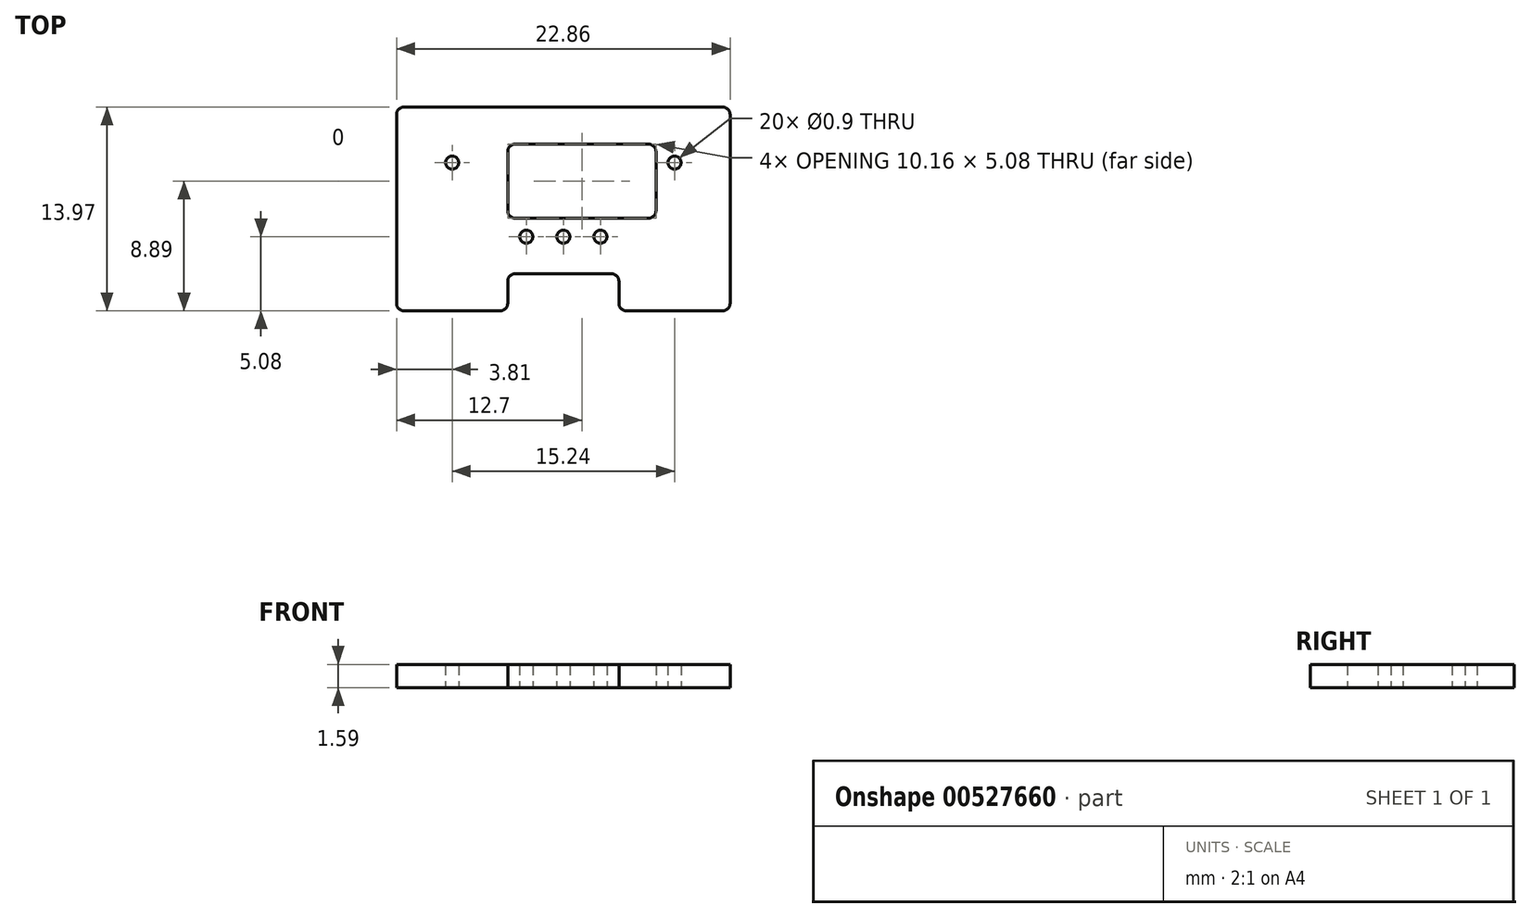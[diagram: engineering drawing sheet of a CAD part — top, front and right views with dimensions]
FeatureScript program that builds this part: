
annotation { "Feature Type Name" : "Feature", "Feature Type Description" : "" }
export const myFeature = defineFeature(function(context is Context, id is Id, definition is map)
    precondition{}
    {
        {
            var Q0;
            Q0=qCreatedBy(makeId("Top.planeOp"),FACE);
            var sketch = newSketch(context, id + "F0", { "sketchPlane" : qUnion([Q0])});
            skPoint(sketch, "E0", {"position": v(0, 0) * mm});
            skPoint(sketch, "E1.0.1.0", {"position": v(0, 2.54) * mm});
            skPoint(sketch, "E1.0.2.0", {"position": v(0, 5.08) * mm});
            skPoint(sketch, "E1.0.3.0", {"position": v(0, 7.62) * mm});
            skPoint(sketch, "E1.0.4.0", {"position": v(0, 10.16) * mm});
            skPoint(sketch, "E1.0.5.0", {"position": v(0, 12.7) * mm});
            skPoint(sketch, "E1.1.0.0", {"position": v(2.54, 0) * mm});
            skPoint(sketch, "E1.1.1.0", {"position": v(2.54, 2.54) * mm});
            skPoint(sketch, "E1.1.2.0", {"position": v(2.54, 5.08) * mm});
            skPoint(sketch, "E1.1.3.0", {"position": v(2.54, 7.62) * mm});
            skPoint(sketch, "E1.1.4.0", {"position": v(2.54, 10.16) * mm});
            skPoint(sketch, "E1.1.5.0", {"position": v(2.54, 12.7) * mm});
            skPoint(sketch, "E1.2.0.0", {"position": v(5.08, 0) * mm});
            skPoint(sketch, "E1.2.1.0", {"position": v(5.08, 2.54) * mm});
            skPoint(sketch, "E1.2.2.0", {"position": v(5.08, 5.08) * mm});
            skPoint(sketch, "E1.2.3.0", {"position": v(5.08, 7.62) * mm});
            skPoint(sketch, "E1.2.4.0", {"position": v(5.08, 10.16) * mm});
            skPoint(sketch, "E1.2.5.0", {"position": v(5.08, 12.7) * mm});
            skPoint(sketch, "E1.3.0.0", {"position": v(7.62, 0) * mm});
            skPoint(sketch, "E1.3.1.0", {"position": v(7.62, 2.54) * mm});
            skPoint(sketch, "E1.3.2.0", {"position": v(7.62, 5.08) * mm});
            skPoint(sketch, "E1.3.3.0", {"position": v(7.62, 7.62) * mm});
            skPoint(sketch, "E1.3.4.0", {"position": v(7.62, 10.16) * mm});
            skPoint(sketch, "E1.3.5.0", {"position": v(7.62, 12.7) * mm});
            skPoint(sketch, "E1.4.0.0", {"position": v(10.16, 0) * mm});
            skPoint(sketch, "E1.4.1.0", {"position": v(10.16, 2.54) * mm});
            skPoint(sketch, "E1.4.2.0", {"position": v(10.16, 5.08) * mm});
            skPoint(sketch, "E1.4.3.0", {"position": v(10.16, 7.62) * mm});
            skPoint(sketch, "E1.4.4.0", {"position": v(10.16, 10.16) * mm});
            skPoint(sketch, "E1.4.5.0", {"position": v(10.16, 12.7) * mm});
            skPoint(sketch, "E1.5.0.0", {"position": v(12.7, 0) * mm});
            skPoint(sketch, "E1.5.1.0", {"position": v(12.7, 2.54) * mm});
            skPoint(sketch, "E1.5.2.0", {"position": v(12.7, 5.08) * mm});
            skPoint(sketch, "E1.5.3.0", {"position": v(12.7, 7.62) * mm});
            skPoint(sketch, "E1.5.4.0", {"position": v(12.7, 10.16) * mm});
            skPoint(sketch, "E1.5.5.0", {"position": v(12.7, 12.7) * mm});
            skPoint(sketch, "E1.6.0.0", {"position": v(15.24, 0) * mm});
            skPoint(sketch, "E1.6.1.0", {"position": v(15.24, 2.54) * mm});
            skPoint(sketch, "E1.6.2.0", {"position": v(15.24, 5.08) * mm});
            skPoint(sketch, "E1.6.3.0", {"position": v(15.24, 7.62) * mm});
            skPoint(sketch, "E1.6.4.0", {"position": v(15.24, 10.16) * mm});
            skPoint(sketch, "E1.6.5.0", {"position": v(15.24, 12.7) * mm});
            skPoint(sketch, "E1.7.0.0", {"position": v(17.78, 0) * mm});
            skPoint(sketch, "E1.7.1.0", {"position": v(17.78, 2.54) * mm});
            skPoint(sketch, "E1.7.2.0", {"position": v(17.78, 5.08) * mm});
            skPoint(sketch, "E1.7.3.0", {"position": v(17.78, 7.62) * mm});
            skPoint(sketch, "E1.7.4.0", {"position": v(17.78, 10.16) * mm});
            skPoint(sketch, "E1.7.5.0", {"position": v(17.78, 12.7) * mm});
            skPoint(sketch, "E1.8.0.0", {"position": v(20.32, 0) * mm});
            skPoint(sketch, "E1.8.1.0", {"position": v(20.32, 2.54) * mm});
            skPoint(sketch, "E1.8.2.0", {"position": v(20.32, 5.08) * mm});
            skPoint(sketch, "E1.8.3.0", {"position": v(20.32, 7.62) * mm});
            skPoint(sketch, "E1.8.4.0", {"position": v(20.32, 10.16) * mm});
            skPoint(sketch, "E1.8.5.0", {"position": v(20.32, 12.7) * mm});
            skLineSegment(sketch, "E1.direction1", {"start": v(0, 0) * mm, "end": v(2.54, 0) * mm, "construction": true});
            skLineSegment(sketch, "E1.direction2", {"start": v(0, 0) * mm, "end": v(0, 2.54) * mm, "construction": true});
            skLineSegment(sketch, "E2.bottom", {"start": v(8.9, 6.35) * mm, "end": v(19.05, 6.35) * mm});
            skLineSegment(sketch, "E2.top", {"start": v(8.9, 11.43) * mm, "end": v(19.05, 11.43) * mm});
            skLineSegment(sketch, "E2.left", {"start": v(8.9, 6.35) * mm, "end": v(8.9, 11.43) * mm});
            skLineSegment(sketch, "E2.right", {"start": v(19.05, 6.35) * mm, "end": v(19.05, 11.43) * mm});
            skPoint(sketch, "E3", {"position": v(19.05, 5.08) * mm});
            skPoint(sketch, "E4", {"position": v(12.7, 6.35) * mm});
            skPoint(sketch, "E5", {"position": v(8.9, 5.08) * mm});
            skPoint(sketch, "E6", {"position": v(12.7, 11.43) * mm});
            skPoint(sketch, "E7.0.0.6", {"position": v(0, 15.24) * mm});
            skPoint(sketch, "E7.0.1.6", {"position": v(2.54, 15.24) * mm});
            skPoint(sketch, "E7.0.2.6", {"position": v(5.08, 15.24) * mm});
            skPoint(sketch, "E7.0.3.6", {"position": v(7.62, 15.24) * mm});
            skPoint(sketch, "E7.0.4.6", {"position": v(10.16, 15.24) * mm});
            skPoint(sketch, "E7.0.5.6", {"position": v(12.7, 15.24) * mm});
            skPoint(sketch, "E7.0.6.6", {"position": v(15.24, 15.24) * mm});
            skPoint(sketch, "E7.0.7.6", {"position": v(17.78, 15.24) * mm});
            skPoint(sketch, "E7.0.8.6", {"position": v(20.32, 15.24) * mm});
            skPoint(sketch, "E8.0.9.0", {"position": v(22.86, 0) * mm});
            skPoint(sketch, "E8.0.9.1", {"position": v(22.86, 2.54) * mm});
            skPoint(sketch, "E8.0.9.2", {"position": v(22.86, 5.08) * mm});
            skPoint(sketch, "E8.0.9.3", {"position": v(22.86, 7.62) * mm});
            skPoint(sketch, "E8.0.9.4", {"position": v(22.86, 10.16) * mm});
            skPoint(sketch, "E8.0.9.5", {"position": v(22.86, 12.7) * mm});
            skPoint(sketch, "E8.0.9.6", {"position": v(22.86, 15.24) * mm});
            skPoint(sketch, "E8.0.10.0", {"position": v(25.4, 0) * mm});
            skPoint(sketch, "E8.0.10.1", {"position": v(25.4, 2.54) * mm});
            skPoint(sketch, "E8.0.10.2", {"position": v(25.4, 5.08) * mm});
            skPoint(sketch, "E8.0.10.3", {"position": v(25.4, 7.62) * mm});
            skPoint(sketch, "E8.0.10.4", {"position": v(25.4, 10.16) * mm});
            skPoint(sketch, "E8.0.10.5", {"position": v(25.4, 12.7) * mm});
            skPoint(sketch, "E8.0.10.6", {"position": v(25.4, 15.24) * mm});
            skCircle(sketch, "E9", {"center": v(12.7, 5.08) * mm, "radius": 0.45 * mm});
            skCircle(sketch, "E10", {"center": v(10.16, 5.08) * mm, "radius": 0.45 * mm});
            skCircle(sketch, "E11", {"center": v(15.24, 5.08) * mm, "radius": 0.45 * mm});
            skCircle(sketch, "E12", {"center": v(20.32, 10.16) * mm, "radius": 0.45 * mm});
            skCircle(sketch, "E13", {"center": v(5.08, 10.16) * mm, "radius": 0.45 * mm});
            skLineSegment(sketch, "E14", {"start": v(10.16, 5.08) * mm, "end": v(7.62, 5.08) * mm, "construction": true});
            skLineSegment(sketch, "E15", {"start": v(20.32, 5.08) * mm, "end": v(17.78, 5.08) * mm, "construction": true});
            skLineSegment(sketch, "E16", {"start": v(12.7, 7.62) * mm, "end": v(12.7, 5.08) * mm, "construction": true});
            skLineSegment(sketch, "E17", {"start": v(12.7, 12.7) * mm, "end": v(12.7, 10.16) * mm, "construction": true});
            skLineSegment(sketch, "E18", {"start": v(25.4, 5.08) * mm, "end": v(22.86, 5.08) * mm, "construction": true});
            skLineSegment(sketch, "E19", {"start": v(2.54, 5.08) * mm, "end": v(0, 5.08) * mm, "construction": true});
            skLineSegment(sketch, "E20", {"start": v(12.7, 15.24) * mm, "end": v(12.7, 12.7) * mm, "construction": true});
            skPoint(sketch, "E21", {"position": v(12.7, 13.97) * mm});
            skPoint(sketch, "E22", {"position": v(24.13, 5.08) * mm});
            skPoint(sketch, "E23", {"position": v(1.27, 5.08) * mm});
            skLineSegment(sketch, "E24.bottom", {"start": v(24.13, 13.97) * mm, "end": v(1.27, 13.97) * mm});
            skLineSegment(sketch, "E24.top", {"start": v(24.13, 0) * mm, "end": v(16.51, 0) * mm});
            skLineSegment(sketch, "E24.left", {"start": v(24.13, 13.97) * mm, "end": v(24.13, 0) * mm});
            skLineSegment(sketch, "E24.right", {"start": v(1.27, 13.97) * mm, "end": v(1.27, 0) * mm});
            skLineSegment(sketch, "E25", {"start": v(8.9, 2.54) * mm, "end": v(8.9, 0) * mm});
            skLineSegment(sketch, "E26", {"start": v(17.78, 10.16) * mm, "end": v(15.24, 10.16) * mm, "construction": true});
            skPoint(sketch, "E27", {"position": v(16.51, 10.16) * mm});
            skLineSegment(sketch, "E28", {"start": v(8.9, 2.54) * mm, "end": v(16.51, 2.54) * mm});
            skLineSegment(sketch, "E29", {"start": v(16.51, 2.54) * mm, "end": v(16.51, 0) * mm});
            skLineSegment(sketch, "E30.trimOffspring", {"start": v(8.9, 0) * mm, "end": v(1.27, 0) * mm});
            skSolve(sketch);
        }
        {
            assignVariable(context, id + "F1", {"name" : "rf", "anyValue" : 0.5 * mm});
        }
        {
            assignVariable(context, id + "F2", {"name" : "rt", "anyValue" : 1.59 * mm});
        }
        {
            var Q0;
            Q0 = qSketchRegion(id + "F0", true);
            extrude(context, id + "F3", {"entities" : qUnion([Q0]), "depth" : getVariable(context, 'rt'), "offsetDistance" : 25.4 * mm});
        }
        {
            var Q0;
            Q0=makeQuery(id+"F3.opExtrude","SWEPT_EDGE",EDGE,{"disambiguationData":[OSD([sQuery(id+"F0.wireOp",EDGE,"E24.right"),sQuery(id+"F0.wireOp",EDGE,"E30.trimOffspring")])]});
            var Q1;
            Q1=makeQuery(id+"F3.opExtrude","SWEPT_EDGE",EDGE,{"disambiguationData":[OSD([sQuery(id+"F0.wireOp",EDGE,"E25"),sQuery(id+"F0.wireOp",EDGE,"E30.trimOffspring")])]});
            var Q2;
            Q2=makeQuery(id+"F3.opExtrude","SWEPT_EDGE",EDGE,{"disambiguationData":[OSD([sQuery(id+"F0.wireOp",EDGE,"E28"),sQuery(id+"F0.wireOp",EDGE,"E29")])]});
            var Q3;
            Q3=makeQuery(id+"F3.opExtrude","SWEPT_EDGE",EDGE,{"disambiguationData":[OSD([sQuery(id+"F0.wireOp",EDGE,"E24.top"),sQuery(id+"F0.wireOp",EDGE,"E29")])]});
            var Q4;
            Q4=makeQuery(id+"F3.opExtrude","SWEPT_EDGE",EDGE,{"disambiguationData":[OSD([sQuery(id+"F0.wireOp",EDGE,"E24.top"),sQuery(id+"F0.wireOp",EDGE,"E24.left")])]});
            var Q5;
            Q5=makeQuery(id+"F3.opExtrude","SWEPT_EDGE",EDGE,{"disambiguationData":[OSD([sQuery(id+"F0.wireOp",EDGE,"E2.top"),sQuery(id+"F0.wireOp",EDGE,"E2.left")])]});
            var Q6;
            Q6=makeQuery(id+"F3.opExtrude","SWEPT_EDGE",EDGE,{"disambiguationData":[OSD([sQuery(id+"F0.wireOp",EDGE,"E25"),sQuery(id+"F0.wireOp",EDGE,"E28")])]});
            var Q7;
            Q7=makeQuery(id+"F3.opExtrude","SWEPT_EDGE",EDGE,{"disambiguationData":[OSD([sQuery(id+"F0.wireOp",EDGE,"E24.bottom"),sQuery(id+"F0.wireOp",EDGE,"E24.left")])]});
            var Q8;
            Q8=makeQuery(id+"F3.opExtrude","SWEPT_EDGE",EDGE,{"disambiguationData":[OSD([sQuery(id+"F0.wireOp",EDGE,"E2.bottom"),sQuery(id+"F0.wireOp",EDGE,"E2.left")])]});
            var Q9;
            Q9=makeQuery(id+"F3.opExtrude","SWEPT_EDGE",EDGE,{"disambiguationData":[OSD([sQuery(id+"F0.wireOp",EDGE,"E24.bottom"),sQuery(id+"F0.wireOp",EDGE,"E24.right")])]});
            var Q10;
            Q10=makeQuery(id+"F3.opExtrude","SWEPT_EDGE",EDGE,{"disambiguationData":[OSD([sQuery(id+"F0.wireOp",EDGE,"E2.bottom"),sQuery(id+"F0.wireOp",EDGE,"E2.right")])]});
            var Q11;
            Q11=makeQuery(id+"F3.opExtrude","SWEPT_EDGE",EDGE,{"disambiguationData":[OSD([sQuery(id+"F0.wireOp",EDGE,"E2.top"),sQuery(id+"F0.wireOp",EDGE,"E2.right")])]});
            fillet(context, id + "F4", {"entities" : qUnion([Q0, Q1, Q2, Q3, Q4, Q5, Q6, Q7, Q8, Q9, Q10, Q11]), "radius" : getVariable(context, 'rf'), "tangentPropagation" : true, "allowEdgeOverflow" : false});
        }
    });
